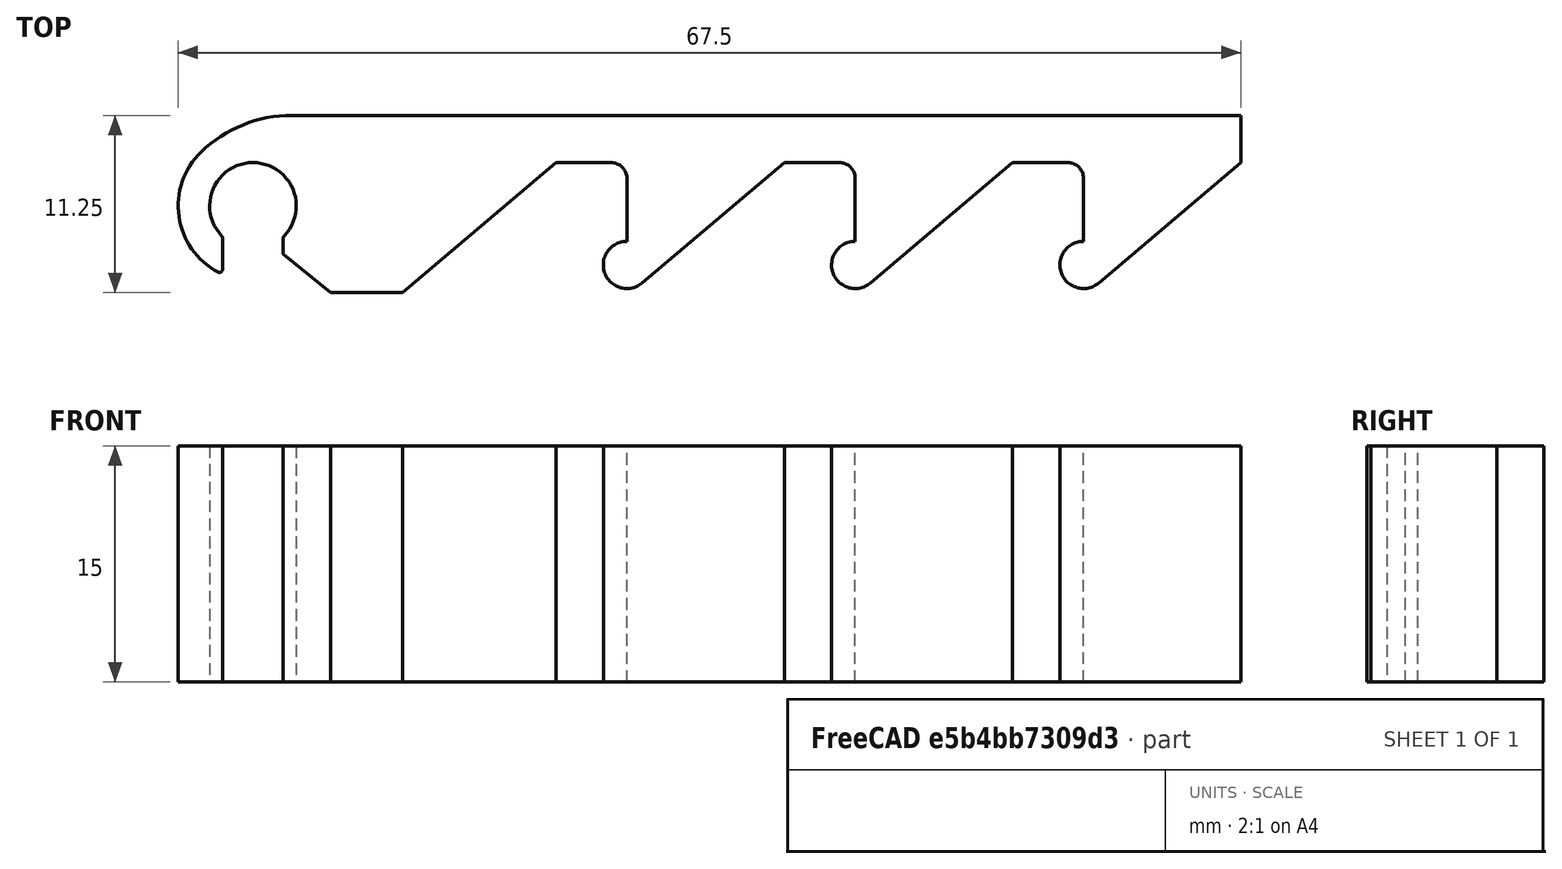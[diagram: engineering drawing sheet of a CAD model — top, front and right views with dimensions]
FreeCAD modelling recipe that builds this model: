
FCSTD DOCUMENT  (FreeCAD 0.19R24415 (Git))
Label: gr36-bracket
License: All rights reserved
LicenseURL: http://en.wikipedia.org/wiki/All_rights_reserved
objects: Sketcher::SketchObject×1, PartDesign::Pad×1, PartDesign::Body×1
note: 4 computed .brp shape members not serialized (recipe doc carries the construction recipe); baked Part::Feature solids carry a one-line shape summary decoded from their .brp

FEATURE [Sketcher::SketchObject] Sketch
  FullyConstrained = true
  MapMode = 5
  Support = -> [XY_Plane]
  sketch-geometry (39):
    g0: ArcOfCircle CenterX=0 CenterY=0 CenterZ=0 NormalX=0 NormalY=0 NormalZ=1 AngleXU=0 Radius=2.75 StartAngle=5.51668 EndAngle=10.1913
    g1: ArcOfCircle CenterX=0 CenterY=0 CenterZ=0 NormalX=0 NormalY=0 NormalZ=1 AngleXU=0 Radius=4.75 StartAngle=2.33885 EndAngle=4.22646
    g2: LineSegment StartX=1.925 StartY=-2.04619 StartZ=0 EndX=1.925 EndY=-3.04619 EndZ=0
    g3: LineSegment StartX=-1.925 StartY=-2.04619 StartZ=0 EndX=-1.925 EndY=-4.02329 EndZ=0
    g4: ArcOfCircle CenterX=-2.125 CenterY=-4.02329 CenterZ=0 NormalX=0 NormalY=0 NormalZ=1 AngleXU=0 Radius=0.2 StartAngle=4.22646 EndAngle=6.28319
    g5: LineSegment StartX=4.925 StartY=-5.5 StartZ=0 EndX=9.50432 EndY=-5.5 EndZ=0
    g6: LineSegment StartX=4.925 StartY=-5.5 StartZ=0 EndX=1.925 EndY=-3.04619 EndZ=0
    g7: LineSegment StartX=23.75 StartY=2.75 StartZ=0 EndX=-2.75 EndY=2.75 EndZ=0
    g8: LineSegment StartX=-2.75 StartY=2.75 StartZ=0 EndX=-2.75 EndY=0 EndZ=0
    g9: LineSegment StartX=9.50432 StartY=-5.5 StartZ=0 EndX=19.25 EndY=2.75 EndZ=0
    g10: LineSegment StartX=23.75 StartY=1.75 StartZ=0 EndX=23.75 EndY=-2.25 EndZ=0
    g11: LineSegment StartX=23.75 StartY=-2.25 StartZ=0 EndX=23.75 EndY=-3.75 EndZ=0
    g12: LineSegment StartX=19.25 StartY=2.75 StartZ=0 EndX=22.75 EndY=2.75 EndZ=0
    g13: ArcOfCircle CenterX=22.75 CenterY=1.75 CenterZ=0 NormalX=0 NormalY=0 NormalZ=1 AngleXU=0 Radius=1 StartAngle=0 EndAngle=1.5708
    g14: GeomPoint X=23.75 Y=2.75 Z=0
    g15: ArcOfCircle CenterX=23.75 CenterY=-3.75 CenterZ=0 NormalX=0 NormalY=0 NormalZ=1 AngleXU=0 Radius=1.5 StartAngle=1.5708 EndAngle=5.41486
    g16: LineSegment StartX=23.75 StartY=2.75 StartZ=0 EndX=33.75 EndY=2.75 EndZ=0
    g17: LineSegment StartX=33.75 StartY=2.75 StartZ=0 EndX=24.7192 EndY=-4.89487 EndZ=0
    g18: LineSegment StartX=2.4747 StartY=5.75 StartZ=0 EndX=62.75 EndY=5.75 EndZ=0
    g19: ArcOfCircle CenterX=2.4747 CenterY=-2.56207 CenterZ=0 NormalX=0 NormalY=0 NormalZ=1 AngleXU=0 Radius=8.31207 StartAngle=1.5708 EndAngle=2.33885
    g20: ArcOfCircle CenterX=-2.125 CenterY=-2.04619 CenterZ=0 NormalX=0 NormalY=0 NormalZ=1 AngleXU=0 Radius=0.2 StartAngle=0 EndAngle=0.766505
    g21: ArcOfCircle CenterX=2.125 CenterY=-2.04619 CenterZ=0 NormalX=0 NormalY=0 NormalZ=1 AngleXU=0 Radius=0.2 StartAngle=2.37509 EndAngle=3.14159
    g22: LineSegment StartX=38.25 StartY=1.75 StartZ=0 EndX=38.25 EndY=-2.25 EndZ=0
    g23: LineSegment StartX=38.25 StartY=-2.25 StartZ=0 EndX=38.25 EndY=-3.75 EndZ=0
    g24: LineSegment StartX=33.75 StartY=2.75 StartZ=0 EndX=37.25 EndY=2.75 EndZ=0
    g25: ArcOfCircle CenterX=37.25 CenterY=1.75 CenterZ=0 NormalX=0 NormalY=0 NormalZ=1 AngleXU=0 Radius=1 StartAngle=0 EndAngle=1.5708
    g26: GeomPoint X=38.25 Y=2.75 Z=0
    g27: ArcOfCircle CenterX=38.25 CenterY=-3.75 CenterZ=0 NormalX=0 NormalY=0 NormalZ=1 AngleXU=0 Radius=1.5 StartAngle=1.5708 EndAngle=5.41486
    g28: LineSegment StartX=38.25 StartY=2.75 StartZ=0 EndX=48.25 EndY=2.75 EndZ=0
    g29: LineSegment StartX=48.25 StartY=2.75 StartZ=0 EndX=39.2192 EndY=-4.89487 EndZ=0
    g30: LineSegment StartX=52.75 StartY=1.75 StartZ=0 EndX=52.75 EndY=-2.25 EndZ=0
    g31: LineSegment StartX=52.75 StartY=-2.25 StartZ=0 EndX=52.75 EndY=-3.75 EndZ=0
    g32: LineSegment StartX=48.25 StartY=2.75 StartZ=0 EndX=51.75 EndY=2.75 EndZ=0
    g33: ArcOfCircle CenterX=51.75 CenterY=1.75 CenterZ=0 NormalX=0 NormalY=0 NormalZ=1 AngleXU=0 Radius=1 StartAngle=0 EndAngle=1.5708
    g34: GeomPoint X=52.75 Y=2.75 Z=0
    g35: ArcOfCircle CenterX=52.75 CenterY=-3.75 CenterZ=0 NormalX=0 NormalY=0 NormalZ=1 AngleXU=0 Radius=1.5 StartAngle=1.5708 EndAngle=5.41486
    g36: LineSegment StartX=52.75 StartY=2.75 StartZ=0 EndX=62.75 EndY=2.75 EndZ=0
    g37: LineSegment StartX=62.75 StartY=2.75 StartZ=0 EndX=53.7192 EndY=-4.89487 EndZ=0
    g38: LineSegment StartX=62.75 StartY=2.75 StartZ=0 EndX=62.75 EndY=5.75 EndZ=0
  constraints (100):
    c: Coincident(g0,g-1)
    c: Radius(g0) = 2.75
    c: Coincident(g1,g0)
    c: Vertical(g2)
    c: Vertical(g3)
    c: Radius(g1) = 4.75
    c: Tangent(g1,g4) = -1.5708
    c: Tangent(g3,g4) = 1.5708
    c: Radius(g4) = 0.2
    c: Horizontal(g5)
    c: DistanceY(g5,g0) = 5.5
    c: Coincident(g6,g5)
    c: Coincident(g6,g2)
    c: DistanceX(g2,g5) = 3
    c: Horizontal(g7)
    c: Tangent(g0,g7)
    c: Coincident(g8,g7)
    c: Vertical(g8)
    c: Tangent(g8,g0) = -1.5708
    c: DistanceX(g7,g7) = 26.5
    c: Coincident(g9,g5)
    c: PointOnObject(g9,g7)
    c: DistanceX(g9,g7) = 4.5
    c: Coincident(g14,g7)
    c: Vertical(g10)
    c: DistanceY(g10,g14) = 5
    c: Coincident(g11,g10)
    c: Vertical(g11)
    c: Coincident(g12,g9)
    c: PointOnObject(g14,g12)
    c: PointOnObject(g14,g10)
    c: Tangent(g12,g13) = 1.5708
    c: Tangent(g10,g13) = 1.5708
    c: Radius(g13) = 1
    c: Coincident(g15,g11)
    c: Coincident(g15,g10)
    c: Coincident(g16,g7)
    c: Horizontal(g16)
    c: DistanceX(g16,g16) = 10
    c: Coincident(g17,g16)
    c: Tangent(g17,g15) = 1.5708
    c: DistanceY(g11,g11) = 1.5
    c: Horizontal(g18)
    c: Tangent(g18,g19) = 1.5708
    c: Tangent(g1,g19) = -1.5708
    c: Distance(g9,g18) = 3
    c: DistanceX(g1,g0) = 3.3
    c: Tangent(g0,g20) = 1.5708
    c: Tangent(g3,g20) = 1.5708
    c: Distance(g2,g3) = 3.85
    c: Tangent(g0,g21) = 1.5708
    c: Tangent(g2,g21) = -1.5708
    c: Equal(g21,g20)
    c: Radius(g21) = 0.2
    c: Horizontal(g3,g2)
    c: DistanceY(g2,g2) = 1
    c: Vertical(g22)
    c: DistanceY(g22,g26) = 5
    c: Coincident(g23,g22)
    c: Vertical(g23)
    c: PointOnObject(g26,g24)
    c: PointOnObject(g26,g22)
    c: Tangent(g24,g25) = 1.5708
    c: Tangent(g22,g25) = 1.5708
    c: Equal(g13,g25) = 1
    c: Coincident(g27,g23)
    c: Coincident(g27,g22)
    c: Horizontal(g28)
    c: Equal(g16,g28) = 5
    c: Coincident(g29,g28)
    c: Tangent(g29,g27) = 1.5708
    c: Equal(g11,g23) = 1.5
    c: Horizontal(g24)
    c: Coincident(g24,g17)
    c: Equal(g24,g12)
    c: Coincident(g28,g26)
    c: Parallel(g17,g9)
    c: Vertical(g30)
    c: DistanceY(g30,g34) = 5
    c: Coincident(g31,g30)
    c: Vertical(g31)
    c: PointOnObject(g34,g32)
    c: PointOnObject(g34,g30)
    c: Tangent(g32,g33) = 1.5708
    c: Tangent(g30,g33) = 1.5708
    c: Coincident(g35,g31)
    c: Coincident(g35,g30)
    c: Horizontal(g36)
    c: Coincident(g37,g36)
    c: Tangent(g37,g35) = 1.5708
    c: Horizontal(g32)
    c: Coincident(g36,g34)
    c: Coincident(g32,g29)
    c: Equal(g24,g32)
    c: Equal(g28,g36)
    c: Equal(g31,g23)
    c: Equal(g33,g25)
    c: Coincident(g38,g18)
    c: Vertical(g38)
    c: Coincident(g38,g37)
FEATURE [PartDesign::Pad] Pad
  Direction = (1,1,1)
  Length = 15
  Length2 = 100
  Profile = -> Sketch
  Type = 0
FEATURE [PartDesign::Body] Body
  Group = -> [Sketch,Pad]
  Origin = -> Origin
  Tip = -> Pad
